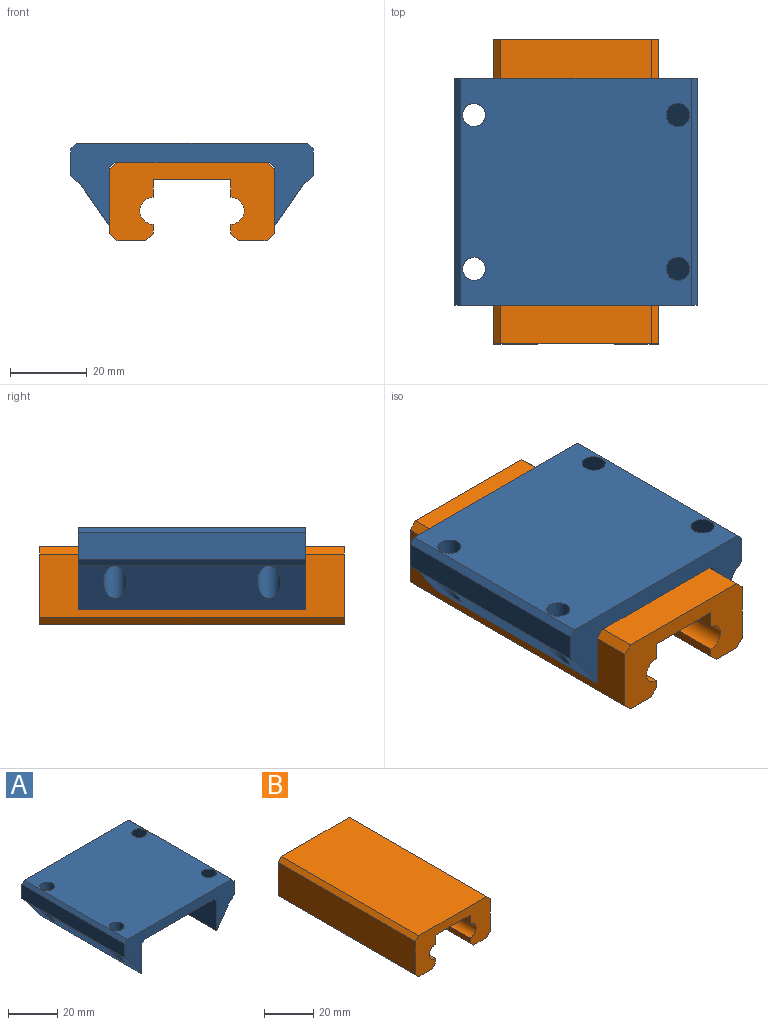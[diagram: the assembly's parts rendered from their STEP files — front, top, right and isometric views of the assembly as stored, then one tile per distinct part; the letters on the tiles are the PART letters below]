
ASSEMBLY  parts=2 mates=1
PART A: 22 faces, bbox 64.8x60.8x23.2 mm
  f0: plane 60.8x13.2mm, normal (-0.82,0,-0.57), area 723.2mm2, adj f1,f9,f10,f11,f18,f19
  f1: plane 59x14.9mm, normal (1,0,0), area 879.1mm2, adj f0,f10,f11,f17
  f2: plane 59x40.01mm, normal (0,0,-1), area 2360.6mm2, adj f10,f11,f16,f17
  f3: plane 59x14.9mm, normal (-1,0,0), area 879mm2, adj f4,f10,f11,f16
  f4: plane 59x11.4mm, normal (0.82,0,-0.57), area 526.4mm2, adj f3,f5,f10,f11,f20,f21
  f5: plane 59x0.5mm, normal (0,0,-1), area 29.5mm2, adj f4,f10,f11,f12
  f6: plane 59x7mm, normal (1,0,0), area 413mm2, adj f10,f11,f12,f14
  f7: plane 60x59mm, normal (0,0,1), area 3426.9mm2, adj f10,f11,f14,f15,f18,f19,f20,f21
  f8: plane 59x7mm, normal (-1,0,0), area 413mm2, adj f10,f11,f13,f15
  f9: plane 59x0.5mm, normal (0,0,-1), area 29.5mm2, adj f0,f10,f11,f13
  f10: plane 63x21.4mm, normal (0,-1,0), area 503.9mm2, adj f0,f1,f2,f3,f4,f5,f6,f7
  f11: plane 63x21.4mm, normal (0,1,0), area 503.9mm2, adj f0,f1,f2,f3,f4,f5,f6,f7
  f12: plane 59x1.5mm, normal (0.71,0,-0.71), area 125.2mm2, adj f5,f6,f10,f11
  f13: plane 59x1.5mm, normal (-0.71,0,-0.71), area 125.2mm2, adj f8,f9,f10,f11
  f14: plane 59x1.5mm, normal (0.71,0,0.71), area 125.2mm2, adj f6,f7,f10,f11
  f15: plane 59x1.5mm, normal (-0.71,0,0.71), area 125.2mm2, adj f7,f8,f10,f11
  f16: plane 59x1.5mm, normal (-0.71,0,-0.71), area 125.2mm2, adj f2,f3,f10,f11
  f17: plane 59x1.5mm, normal (0.71,0,-0.71), area 125.2mm2, adj f1,f2,f10,f11
  f18: cylinder r=3mm len=18.55mm, axis (0,0,1), area 269.1mm2, adj f0,f7
  f19: cylinder r=3mm len=18.55mm, axis (0,0,1), area 269.1mm2, adj f0,f7
  f20: cylinder r=3mm len=18.61mm, axis (0,0,1), area 430.2mm2, adj f4,f7
  f21: cylinder r=3mm len=18.61mm, axis (0,0,1), area 430.2mm2, adj f4,f7
PART B: 20 faces, bbox 43x79x20.4 mm
  f0: plane 79x4.58mm, normal (1,0,0), area 361.8mm2, adj f1,f11,f12,f13
  f1: plane 79x20.05mm, normal (0,0,-1), area 1584mm2, adj f0,f2,f12,f13
  f2: plane 79x4.58mm, normal (-1,0,0), area 361.8mm2, adj f1,f3,f12,f13
  f3: cylinder r=3.52mm len=79mm, axis (0,1,0), area 873.6mm2, adj f2,f4,f12,f13
  f4: plane 79x2.28mm, normal (-1,0,0), area 180.1mm2, adj f3,f12,f13,f14
  f5: plane 79x7.48mm, normal (0,0,-1), area 590.5mm2, adj f12,f13,f14,f16
  f6: plane 79x16.4mm, normal (1,0,0), area 1295.6mm2, adj f12,f13,f16,f18
  f7: plane 79x39mm, normal (0,0,1), area 3081mm2, adj f12,f13,f18,f19
  f8: plane 79x16.4mm, normal (-1,0,0), area 1295.6mm2, adj f12,f13,f17,f19
  f9: plane 79x7.48mm, normal (0,0,-1), area 590.5mm2, adj f12,f13,f15,f17
  f10: plane 79x2.28mm, normal (1,0,0), area 180.1mm2, adj f11,f12,f13,f15
  f11: cylinder r=3.52mm len=79mm, axis (0,1,0), area 873.6mm2, adj f0,f10,f12,f13
  f12: plane 43x20.4mm, normal (0,-1,0), area 507.5mm2, adj f0,f1,f2,f3,f4,f5,f6,f7
  f13: plane 43x20.4mm, normal (0,1,0), area 507.5mm2, adj f0,f1,f2,f3,f4,f5,f6,f7
  f14: plane 79x2mm, normal (-0.71,0,-0.71), area 223.4mm2, adj f4,f5,f12,f13
  f15: plane 79x2mm, normal (0.71,0,-0.71), area 223.4mm2, adj f9,f10,f12,f13
  f16: plane 79x2mm, normal (0.71,0,-0.71), area 223.4mm2, adj f5,f6,f12,f13
  f17: plane 79x2mm, normal (-0.71,0,-0.71), area 223.4mm2, adj f8,f9,f12,f13
  f18: plane 79x2mm, normal (0.71,0,0.71), area 223.4mm2, adj f6,f7,f12,f13
  f19: plane 79x2mm, normal (-0.71,0,0.71), area 223.4mm2, adj f7,f8,f12,f13
PLACE A t=(-5.04,16.87,-1.66)mm
PLACE B t=(-5.03,16.87,-1.66)mm
MATE fastened A.f2 <-> B.f7  axis (0,0,-1) through (16.47,16.87,18.74)mm
